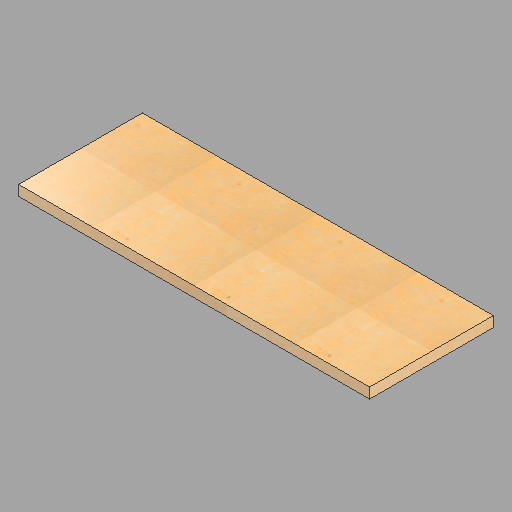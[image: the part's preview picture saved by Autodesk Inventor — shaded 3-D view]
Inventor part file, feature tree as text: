
AUTODESK INVENTOR PART (.ipt)
format: ipt  version: 2023 (Build 270158030, 158C)  size: 211,968 bytes
history: native  units: in
note: dims shown in document units (in); Inventor stores cm internally (conversion verified against a paired STEP export)
features: extrude x1, sketch x1
ambient origin geometry x8: Origin, YZ Plane, XZ Plane, XY Plane, X Axis, Y Axis, Z Axis, Center Point
bodies: Solid1 (feature_tree)
feature tree (2):
  extrude  "Extrusion1"  Depth=35.625in
  sketch  "Sketch1"  dims[d0=101.0in d1=35.625in d2=3.0in d3=0.0in]
